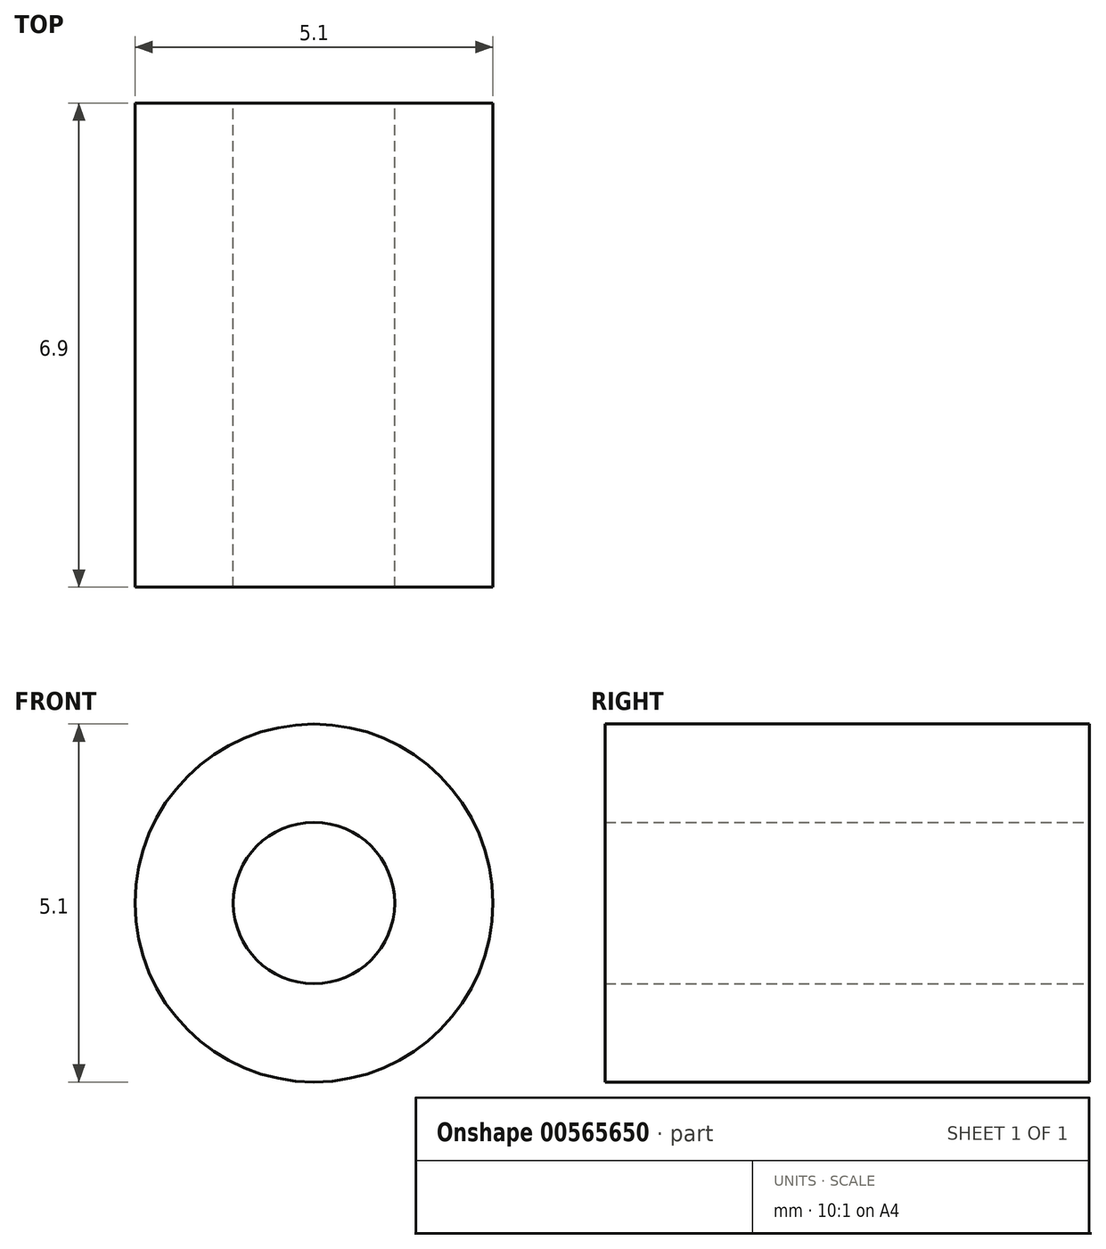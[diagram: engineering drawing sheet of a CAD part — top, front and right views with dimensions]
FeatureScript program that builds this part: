
annotation { "Feature Type Name" : "Feature", "Feature Type Description" : "" }
export const myFeature = defineFeature(function(context is Context, id is Id, definition is map)
    precondition{}
    {
        {
            assignVariable(context, id + "F0", {"name" : "Length", "anyValue" : 6.9});
        }
        {
            var Q0;
            Q0=qCreatedBy(makeId("Front.planeOp"),FACE);
            var sketch = newSketch(context, id + "F1", { "sketchPlane" : qUnion([Q0])});
            skCircle(sketch, "E0", {"center": v(0, 0) * mm, "radius": 1.15 * mm});
            skCircle(sketch, "E1.0", {"center": v(0, 0) * mm, "radius": 2.55 * mm});
            skSolve(sketch);
        }
        {
            var Q0;
            Q0=makeQuery(id+"F1.imprint","IMPRINT",FACE,{"disambiguationData":[TD([[makeQuery(id+"F1.imprint","IMPRINT",EDGE,{"derivedFrom":sQuery(id+"F1.wireOp",EDGE,"E0")}),-1.0]])]});
            extrude(context, id + "F2", {"entities" : qUnion([Q0]), "depth" : (getVariable(context, 'Length')) * mm, "offsetDistance" : 25 * mm});
        }
    });
